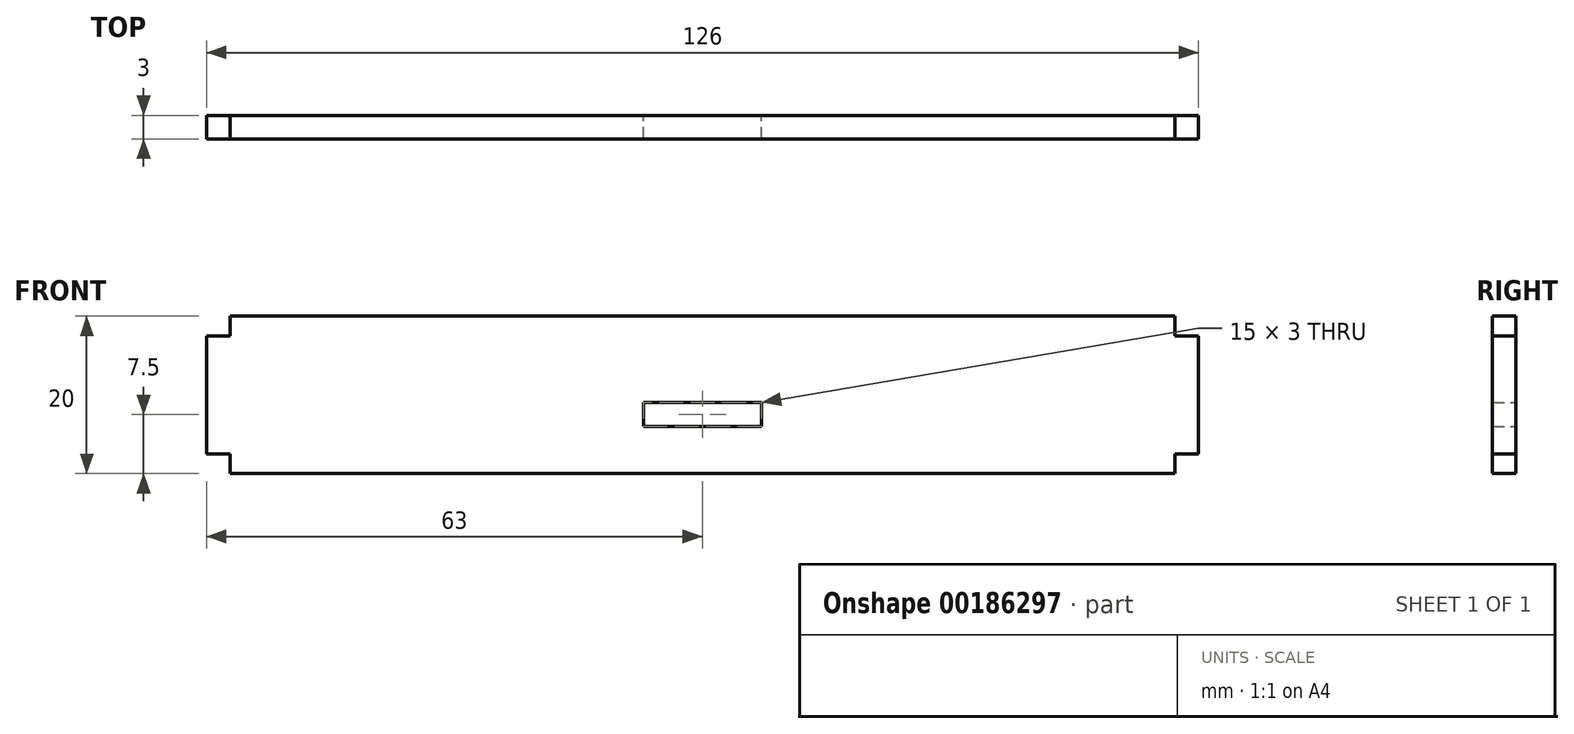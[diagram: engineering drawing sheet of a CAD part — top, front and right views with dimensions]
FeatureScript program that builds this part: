
annotation { "Feature Type Name" : "Feature", "Feature Type Description" : "" }
export const myFeature = defineFeature(function(context is Context, id is Id, definition is map)
    precondition{}
    {
        {
            var Q0;
            Q0=qCreatedBy(makeId("Front.planeOp"),FACE);
            var sketch = newSketch(context, id + "F0", { "sketchPlane" : qUnion([Q0])});
            skLineSegment(sketch, "E0.bottom", {"start": v(-60, 10) * mm, "end": v(60, 10) * mm});
            skLineSegment(sketch, "E0.top", {"start": v(-60, -10) * mm, "end": v(60, -10) * mm});
            skLineSegment(sketch, "E0.left", {"start": v(-60, 10) * mm, "end": v(-60, 7.5) * mm});
            skLineSegment(sketch, "E0.right", {"start": v(60, 10) * mm, "end": v(60, 7.5) * mm});
            skLineSegment(sketch, "E1.trimOffspring", {"start": v(-60, -7.5) * mm, "end": v(-60, -10) * mm});
            skLineSegment(sketch, "E2.trimOffspring", {"start": v(60, -7.5) * mm, "end": v(60, -10) * mm});
            skLineSegment(sketch, "E3", {"start": v(-60, 10) * mm, "end": v(60, -10) * mm, "construction": true});
            skLineSegment(sketch, "E4", {"start": v(60, 10) * mm, "end": v(-60, -10) * mm, "construction": true});
            skLineSegment(sketch, "E5.bottom", {"start": v(-63, 7.5) * mm, "end": v(-60, 7.5) * mm});
            skLineSegment(sketch, "E5.top", {"start": v(-63, -7.5) * mm, "end": v(-60, -7.5) * mm});
            skLineSegment(sketch, "E5.left", {"start": v(-63, 7.5) * mm, "end": v(-63, -7.5) * mm});
            skLineSegment(sketch, "E5.right", {"start": v(63, 7.5) * mm, "end": v(63, -7.5) * mm});
            skLineSegment(sketch, "E6.trimOffspring", {"start": v(60, 7.5) * mm, "end": v(63, 7.5) * mm});
            skLineSegment(sketch, "E7.trimOffspring", {"start": v(60, -7.5) * mm, "end": v(63, -7.5) * mm});
            skPoint(sketch, "E8", {"position": v(0, 0) * mm});
            skLineSegment(sketch, "E9", {"start": v(-63, 0) * mm, "end": v(0, 0) * mm, "construction": true});
            skLineSegment(sketch, "E10.bottom", {"start": v(-7.5, -1) * mm, "end": v(7.5, -1) * mm});
            skLineSegment(sketch, "E10.top", {"start": v(-7.5, -4) * mm, "end": v(7.5, -4) * mm});
            skLineSegment(sketch, "E10.left", {"start": v(-7.5, -1) * mm, "end": v(-7.5, -4) * mm});
            skLineSegment(sketch, "E10.right", {"start": v(7.5, -1) * mm, "end": v(7.5, -4) * mm});
            skLineSegment(sketch, "E11", {"start": v(0, 0) * mm, "end": v(0, -16.84) * mm, "construction": true});
            skPoint(sketch, "E12", {"position": v(-7.5, -2.5) * mm});
            skSolve(sketch);
        }
        {
            var Q0;
            Q0=qSketchRegion(id+"F0",true);
            extrude(context, id + "F1", {"entities" : qUnion([Q0]), "depth" : 3 * mm});
        }
    });
